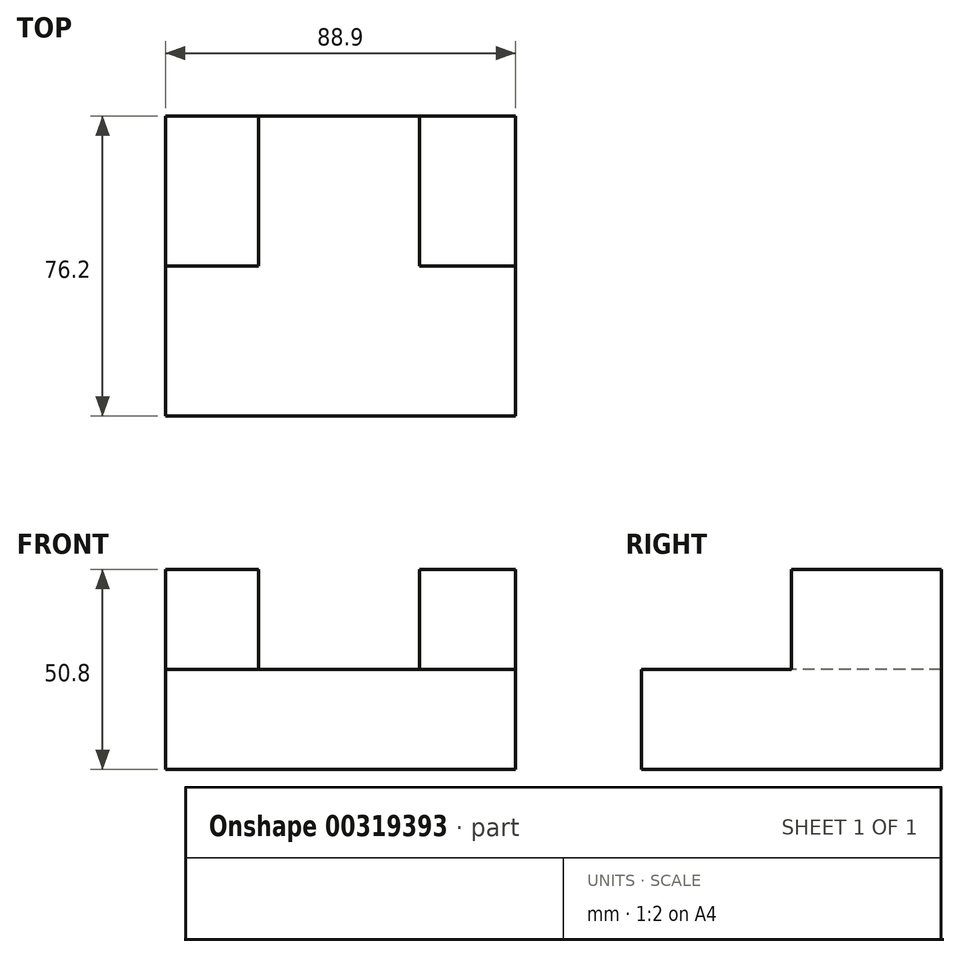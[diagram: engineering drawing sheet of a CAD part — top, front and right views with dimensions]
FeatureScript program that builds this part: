
annotation { "Feature Type Name" : "Feature", "Feature Type Description" : "" }
export const myFeature = defineFeature(function(context is Context, id is Id, definition is map)
    precondition{}
    {
        {
            var Q0;
            Q0=qCreatedBy(makeId("Right.planeOp"),FACE);
            var sketch = newSketch(context, id + "F0", { "sketchPlane" : qUnion([Q0])});
            skLineSegment(sketch, "E0", {"start": v(-44.14, -41.97) * mm, "end": v(32.06, -41.97) * mm});
            skLineSegment(sketch, "E1", {"start": v(32.06, -41.97) * mm, "end": v(32.06, 8.83) * mm});
            skLineSegment(sketch, "E2", {"start": v(32.06, 8.83) * mm, "end": v(-6.04, 8.83) * mm});
            skLineSegment(sketch, "E3", {"start": v(-6.04, 8.83) * mm, "end": v(-6.04, -16.57) * mm});
            skLineSegment(sketch, "E4", {"start": v(-6.04, -16.57) * mm, "end": v(-44.14, -16.57) * mm});
            skLineSegment(sketch, "E5", {"start": v(-44.14, -16.57) * mm, "end": v(-44.14, -41.97) * mm});
            skSolve(sketch);
        }
        {
            var Q0;
            Q0=makeQuery(id+"F0.imprint","IMPRINT",FACE,{"disambiguationData":[TD([[makeQuery(id+"F0.imprint","IMPRINT",EDGE,{"derivedFrom":sQuery(id+"F0.wireOp",EDGE,"E0")}),1.0]])]});
            extrude(context, id + "F1", {"entities" : qUnion([Q0]), "depth" : 88.9 * mm});
        }
        {
            var Q0;
            Q0=makeQuery(id+"F1.opExtrude","SWEPT_FACE",FACE,{"disambiguationData":[OSD([sQuery(id+"F0.wireOp",EDGE,"E3")])]});
            var sketch = newSketch(context, id + "F2", { "sketchPlane" : qUnion([Q0])});
            skLineSegment(sketch, "E6", {"start": v(23.68, 8.83) * mm, "end": v(23.68, -16.57) * mm});
            skLineSegment(sketch, "E7", {"start": v(64.54, 8.83) * mm, "end": v(64.54, -16.57) * mm});
            skSolve(sketch);
        }
        {
            var Q0;
            {var subQ0=sQuery(id+"F2.wireOp",EDGE,"E6");Q0=makeQuery(id+"F2.imprint","IMPRINT",FACE,{"disambiguationData":[TD([[makeQuery(id+"F2.imprint","IMPRINT",EDGE,{"derivedFrom":subQ0}),1.0]])]});}
            extrude(context, id + "F3", {"entities" : qUnion([Q0]), "operationType" : NewBodyOperationType.REMOVE, "endBound" : BoundingType.THROUGH_ALL, "oppositeDirection" : true, "depth" : 25.4 * mm});
        }
    });
